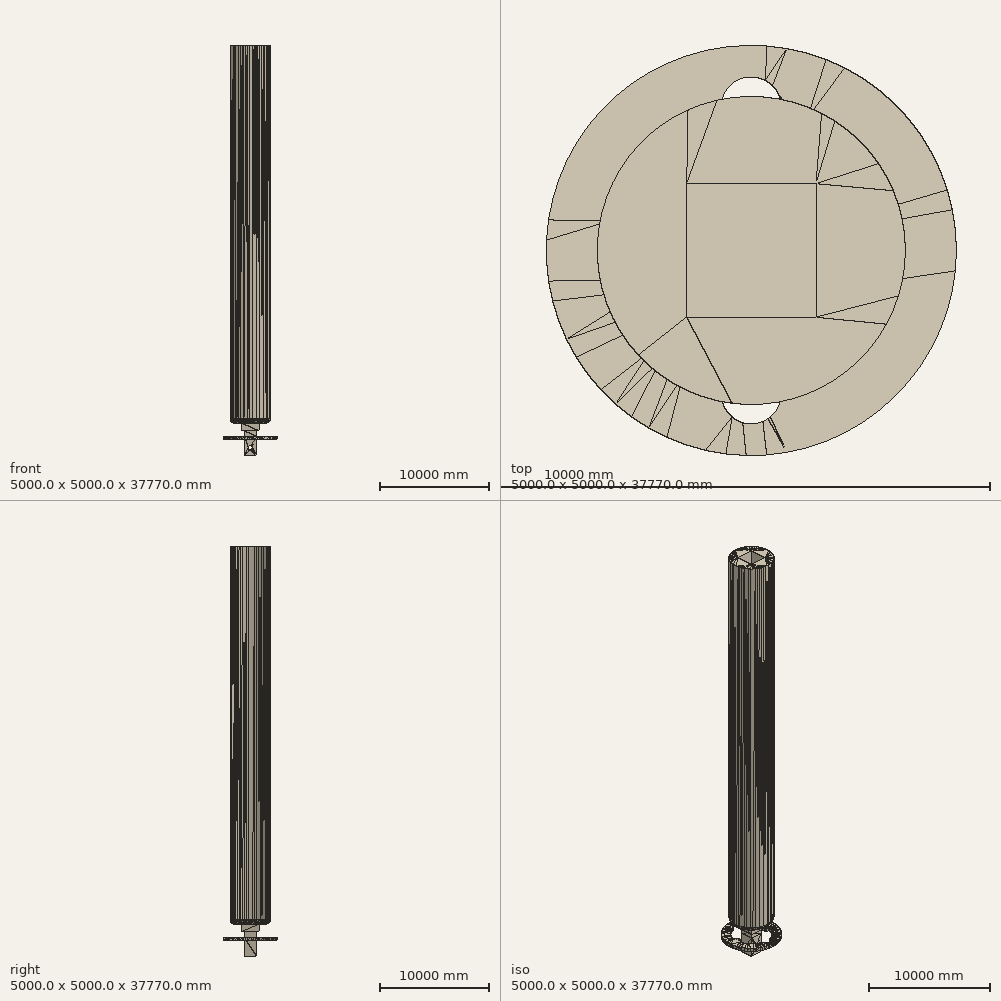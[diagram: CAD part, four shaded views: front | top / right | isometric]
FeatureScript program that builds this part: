
annotation { "Feature Type Name" : "Feature", "Feature Type Description" : "" }
export const myFeature = defineFeature(function(context is Context, id is Id, definition is map)
    precondition{}
    {
        {
            var Q0;
            Q0=qCreatedBy(makeId("Top.planeOp"),FACE);
            var sketch = newSketch(context, id + "F0", { "sketchPlane" : qUnion([Q0])});
            skCircle(sketch, "E0", {"center": v(0, 0) * mm, "radius": 2500 * mm});
            skLineSegment(sketch, "E1.bottom", {"start": v(788.41, -814.1) * mm, "end": v(-788.41, -814.1) * mm});
            skLineSegment(sketch, "E1.top", {"start": v(788.41, 814.1) * mm, "end": v(-788.41, 814.1) * mm});
            skLineSegment(sketch, "E1.left", {"start": v(788.41, -814.1) * mm, "end": v(788.41, 814.1) * mm});
            skLineSegment(sketch, "E1.right", {"start": v(-788.41, -814.1) * mm, "end": v(-788.41, 814.1) * mm});
            skSolve(sketch);
        }
        {
            var Q0;
            Q0=makeQuery(id+"F0.imprint","IMPRINT",FACE,{"disambiguationData":[TD([[makeQuery(id+"F0.imprint","IMPRINT",EDGE,{"derivedFrom":sQuery(id+"F0.wireOp",EDGE,"E0")}),1.0]])]});
            extrude(context, id + "F1", {"entities" : qUnion([Q0]), "depth" : 300 * mm, "offsetDistance" : 25 * mm});
        }
        {
            var Q0;
            Q0=makeQuery(id+"F1.opExtrude","CAP_FACE",FACE,{"disambiguationData":[OSD([sQuery(id+"F0.wireOp",EDGE,"E0"),sQuery(id+"F0.wireOp",EDGE,"E1.bottom"),sQuery(id+"F0.wireOp",EDGE,"E1.top"),sQuery(id+"F0.wireOp",EDGE,"E1.left"),sQuery(id+"F0.wireOp",EDGE,"E1.right")])],"isStart":false});
            var sketch = newSketch(context, id + "F2", { "sketchPlane" : qUnion([Q0])});
            skLineSegment(sketch, "E2.bottom", {"start": v(788.41, -814.1) * mm, "end": v(-788.41, -814.1) * mm});
            skLineSegment(sketch, "E2.top", {"start": v(788.41, 814.1) * mm, "end": v(-788.41, 814.1) * mm});
            skLineSegment(sketch, "E2.left", {"start": v(788.41, -814.1) * mm, "end": v(788.41, 814.1) * mm});
            skLineSegment(sketch, "E2.right", {"start": v(-788.41, -814.1) * mm, "end": v(-788.41, 814.1) * mm});
            skPoint(sketch, "E2.middle", {"position": v(0, 0) * mm});
            skSolve(sketch);
        }
        {
            var Q0;
            Q0=makeQuery(id+"F2.imprint","IMPRINT",FACE,{"disambiguationData":[TD([[makeQuery(id+"F2.imprint","IMPRINT",EDGE,{"derivedFrom":sQuery(id+"F2.wireOp",EDGE,"E2.bottom")}),-1.0]])]});
            extrude(context, id + "F3", {"entities" : qUnion([Q0]), "depth" : 1210 * mm, "offsetDistance" : 25 * mm});
        }
        {
            var Q0;
            Q0=makeQuery(id+"F3.opExtrude","CAP_FACE",FACE,{"disambiguationData":[OSD([sQuery(id+"F2.wireOp",EDGE,"E2.bottom"),sQuery(id+"F2.wireOp",EDGE,"E2.top"),sQuery(id+"F2.wireOp",EDGE,"E2.left"),sQuery(id+"F2.wireOp",EDGE,"E2.right")])],"isStart":true});
            extrude(context, id + "F4", {"entities" : qUnion([Q0]), "depth" : 1760 * mm, "offsetDistance" : 25 * mm});
        }
        {
            var Q0;
            Q0=makeQuery(id+"F4.opExtrude","CAP_EDGE",EDGE,{"disambiguationData":[OSD([sQuery(id+"F2.wireOp",EDGE,"E2.left")])],"isStart":false});
            var Q1;
            Q1=makeQuery(id+"F4.opExtrude","CAP_EDGE",EDGE,{"disambiguationData":[OSD([sQuery(id+"F2.wireOp",EDGE,"E2.bottom")])],"isStart":false});
            var Q2;
            Q2=makeQuery(id+"F4.opExtrude","CAP_EDGE",EDGE,{"disambiguationData":[OSD([sQuery(id+"F2.wireOp",EDGE,"E2.top")])],"isStart":false});
            var Q3;
            Q3=makeQuery(id+"F4.opExtrude","CAP_EDGE",EDGE,{"disambiguationData":[OSD([sQuery(id+"F2.wireOp",EDGE,"E2.right")])],"isStart":false});
            chamfer(context, id + "F5", {"entities" : qUnion([Q0, Q1, Q2, Q3]), "chamferType" : ChamferType.OFFSET_ANGLE, "width" : 400 * mm, "oppositeDirection" : false, "angle" : 30 * degree, "tangentPropagation" : true});
        }
        {
            var Q0;
            Q0=makeQuery(id+"F4.opExtrude","SWEPT_FACE",FACE,{"disambiguationData":[OSD([sQuery(id+"F2.wireOp",EDGE,"E2.bottom")])]});
            var sketch = newSketch(context, id + "F6", { "sketchPlane" : qUnion([Q0])});
            skCircle(sketch, "E3", {"center": v(0, -748.88) * mm, "radius": 178.65 * mm});
            skSolve(sketch);
        }
        {
            var Q0;
            Q0=makeQuery(id+"F6.imprint","IMPRINT",FACE,{"disambiguationData":[TD([[makeQuery(id+"F6.imprint","IMPRINT",EDGE,{"derivedFrom":sQuery(id+"F6.wireOp",EDGE,"E3")}),1.0]])]});
            extrude(context, id + "F7", {"entities" : qUnion([Q0]), "operationType" : NewBodyOperationType.REMOVE, "oppositeDirection" : true, "depth" : 2980 * mm, "offsetDistance" : 25 * mm});
        }
        {
            var Q0;
            Q0=makeQuery(id+"F3.opExtrude","CAP_FACE",FACE,{"disambiguationData":[OSD([sQuery(id+"F2.wireOp",EDGE,"E2.bottom"),sQuery(id+"F2.wireOp",EDGE,"E2.top"),sQuery(id+"F2.wireOp",EDGE,"E2.left"),sQuery(id+"F2.wireOp",EDGE,"E2.right")])],"isStart":false});
            var sketch = newSketch(context, id + "F8", { "sketchPlane" : qUnion([Q0])});
            skCircle(sketch, "E4", {"center": v(0, 0) * mm, "radius": 1877.94 * mm});
            skSolve(sketch);
        }
        {
            var Q0;
            Q0=makeQuery(id+"F8.imprint","IMPRINT",FACE,{"disambiguationData":[TD([[makeQuery(id+"F8.imprint","IMPRINT",EDGE,{"derivedFrom":sQuery(id+"F8.wireOp",EDGE,"E4")}),1.0]])]});
            extrude(context, id + "F9", {"entities" : qUnion([Q0]), "depth" : 34800 * mm, "offsetDistance" : 25 * mm});
        }
        {
            var Q0;
            Q0=makeQuery(id+"F9.opExtrude","CAP_EDGE",EDGE,{"disambiguationData":[OSD([sQuery(id+"F8.wireOp",EDGE,"E4")])],"isStart":true});
            fillet(context, id + "F10", {"entities" : qUnion([Q0]), "radius" : 410.42 * mm, "tangentPropagation" : true, "allowEdgeOverflow" : false});
        }
        {
            var Q0;
            Q0=makeQuery(id+"F4.opExtrude","CAP_FACE",FACE,{"disambiguationData":[OSD([sQuery(id+"F2.wireOp",EDGE,"E2.bottom"),sQuery(id+"F2.wireOp",EDGE,"E2.top"),sQuery(id+"F2.wireOp",EDGE,"E2.left"),sQuery(id+"F2.wireOp",EDGE,"E2.right")])],"isStart":false});
            var sketch = newSketch(context, id + "F11", { "sketchPlane" : qUnion([Q0])});
            skCircle(sketch, "E5", {"center": v(0, 0) * mm, "radius": 1750 * mm});
            skCircle(sketch, "E6", {"center": v(0, 1750) * mm, "radius": 365 * mm});
            skCircle(sketch, "E7", {"center": v(1750, 0) * mm, "radius": 365 * mm});
            skCircle(sketch, "E8", {"center": v(0, -1750) * mm, "radius": 365 * mm});
            skCircle(sketch, "E9", {"center": v(-1750, 0) * mm, "radius": 365 * mm});
            skSolve(sketch);
        }
        {
            var Q0;
            {var subQ0=sQuery(id+"F11.wireOp",EDGE,"E9");var subQ1=sQuery(id+"F11.wireOp",EDGE,"E5");var subQ2=makeQuery(id+"F11.imprint","INTERSECT",VERTEX,{"disambiguationData":[OD(0.0)],"derivedFrom":[subQ1,subQ0]});Q0=makeQuery(id+"F11.imprint","IMPRINT",FACE,{"disambiguationData":[TD([[makeQuery(id+"F11.imprint","IMPRINT",EDGE,{"disambiguationData":[TD([[subQ2,-1.0]])],"derivedFrom":subQ1}),1.0]])]});}
            var Q1;
            {var subQ0=sQuery(id+"F11.wireOp",EDGE,"E9");var subQ1=sQuery(id+"F11.wireOp",EDGE,"E5");var subQ2=makeQuery(id+"F11.imprint","INTERSECT",VERTEX,{"disambiguationData":[OD(0.0)],"derivedFrom":[subQ1,subQ0]});Q1=makeQuery(id+"F11.imprint","IMPRINT",FACE,{"disambiguationData":[TD([[makeQuery(id+"F11.imprint","IMPRINT",EDGE,{"disambiguationData":[TD([[subQ2,-1.0]])],"derivedFrom":subQ1}),-1.0]])]});}
            var Q2;
            {var subQ0=sQuery(id+"F11.wireOp",EDGE,"E6");var subQ1=sQuery(id+"F11.wireOp",EDGE,"E5");var subQ2=makeQuery(id+"F11.imprint","INTERSECT",VERTEX,{"disambiguationData":[OD(0.0)],"derivedFrom":[subQ1,subQ0]});Q2=makeQuery(id+"F11.imprint","IMPRINT",FACE,{"disambiguationData":[TD([[makeQuery(id+"F11.imprint","IMPRINT",EDGE,{"disambiguationData":[TD([[subQ2,-1.0]])],"derivedFrom":subQ1}),1.0]])]});}
            var Q3;
            {var subQ0=sQuery(id+"F11.wireOp",EDGE,"E6");var subQ1=sQuery(id+"F11.wireOp",EDGE,"E5");var subQ2=makeQuery(id+"F11.imprint","INTERSECT",VERTEX,{"disambiguationData":[OD(0.0)],"derivedFrom":[subQ1,subQ0]});Q3=makeQuery(id+"F11.imprint","IMPRINT",FACE,{"disambiguationData":[TD([[makeQuery(id+"F11.imprint","IMPRINT",EDGE,{"disambiguationData":[TD([[subQ2,-1.0]])],"derivedFrom":subQ1}),-1.0]])]});}
            var Q4;
            {var subQ0=sQuery(id+"F11.wireOp",EDGE,"E7");var subQ1=sQuery(id+"F11.wireOp",EDGE,"E5");var subQ2=makeQuery(id+"F11.imprint","INTERSECT",VERTEX,{"disambiguationData":[OD(0.0)],"derivedFrom":[subQ1,subQ0]});Q4=makeQuery(id+"F11.imprint","IMPRINT",FACE,{"disambiguationData":[TD([[makeQuery(id+"F11.imprint","IMPRINT",EDGE,{"disambiguationData":[TD([[subQ2,1.0]])],"derivedFrom":subQ1}),1.0]])]});}
            var Q5;
            {var subQ0=sQuery(id+"F11.wireOp",EDGE,"E7");var subQ1=sQuery(id+"F11.wireOp",EDGE,"E5");var subQ2=makeQuery(id+"F11.imprint","INTERSECT",VERTEX,{"disambiguationData":[OD(0.0)],"derivedFrom":[subQ1,subQ0]});Q5=makeQuery(id+"F11.imprint","IMPRINT",FACE,{"disambiguationData":[TD([[makeQuery(id+"F11.imprint","IMPRINT",EDGE,{"disambiguationData":[TD([[subQ2,1.0]])],"derivedFrom":subQ1}),-1.0]])]});}
            var Q6;
            {var subQ0=sQuery(id+"F11.wireOp",EDGE,"E8");var subQ1=sQuery(id+"F11.wireOp",EDGE,"E5");var subQ2=makeQuery(id+"F11.imprint","INTERSECT",VERTEX,{"disambiguationData":[OD(0.0)],"derivedFrom":[subQ1,subQ0]});Q6=makeQuery(id+"F11.imprint","IMPRINT",FACE,{"disambiguationData":[TD([[makeQuery(id+"F11.imprint","IMPRINT",EDGE,{"disambiguationData":[TD([[subQ2,-1.0]])],"derivedFrom":subQ1}),1.0]])]});}
            var Q7;
            {var subQ0=sQuery(id+"F11.wireOp",EDGE,"E8");var subQ1=sQuery(id+"F11.wireOp",EDGE,"E5");var subQ2=makeQuery(id+"F11.imprint","INTERSECT",VERTEX,{"disambiguationData":[OD(0.0)],"derivedFrom":[subQ1,subQ0]});Q7=makeQuery(id+"F11.imprint","IMPRINT",FACE,{"disambiguationData":[TD([[makeQuery(id+"F11.imprint","IMPRINT",EDGE,{"disambiguationData":[TD([[subQ2,-1.0]])],"derivedFrom":subQ1}),-1.0]])]});}
            extrude(context, id + "F12", {"entities" : qUnion([Q0, Q1, Q2, Q3, Q4, Q5, Q6, Q7]), "operationType" : NewBodyOperationType.REMOVE, "oppositeDirection" : true, "depth" : 2270 * mm, "offsetDistance" : 25 * mm});
        }
    });
